# Revit family: Bath-Freestanding_Dune-KOHLER-Sunstruck-K-EX34378T
name_source: partatom
category: Plumbing Fixtures
units: mm (PartAtom-declared; Revit-internal decimal feet)

## family parameters
Cut with Voids When Loaded = No
Host = Face
Maintain Annotation Orientation = No
OmniClass Number = 23.31.15.00
Part Type = Normal
Room Calculation Point = No
Round Connector Dimension = Use Diameter
Shared = No

## types (2) — shared parameters
ADA Compliant = No
Assembly Code = D2010500
CW Connection = No
Cold Water Inlet = Cold Water Inlet
Date Modified = 10/30/2025
Default Elevation = 0"
Description = 1.7M GEL COAT Lithocast Bath With Texture
Drain Included = Yes
HW Connection = No
Height = 22 15/16"
Hot Water Inlet = Hot Water Inlet
Length = 66 15/16"
Manufacturer = Kohler Co.
Master Format 2014 = 22 41 19
Master Format 2014 Name = Residential Bathtubs
Material = Lithocast
Product Documentation Link = https://files.kohler.com.cn
Product Name = Sunstruck
Product Page URL = https://www.kohler.com.cn
URL = http://www.kohler.com.cn
Vent Connection = No
Waste Connection = Yes
Waste Water Outlet = Waste Water Outlet
WaterSense Certified = No
Width = 29 1/2"

## per-type parameters (varying)
| type | Finish | Model | Type |
| HW1-Honed White | Kohler-Lithocast-HW1-Honed_White | K-EX34378T-DUN-HW1 | 1 |
| TRF-Truffle | Kohler-Lithocast-TRF-Truffle | K-EX34378T-DUN-TRF | 2 |

## geometry (parser evidence)
native form markers: Sweep x5
no freeform markers — native parametric forms only
